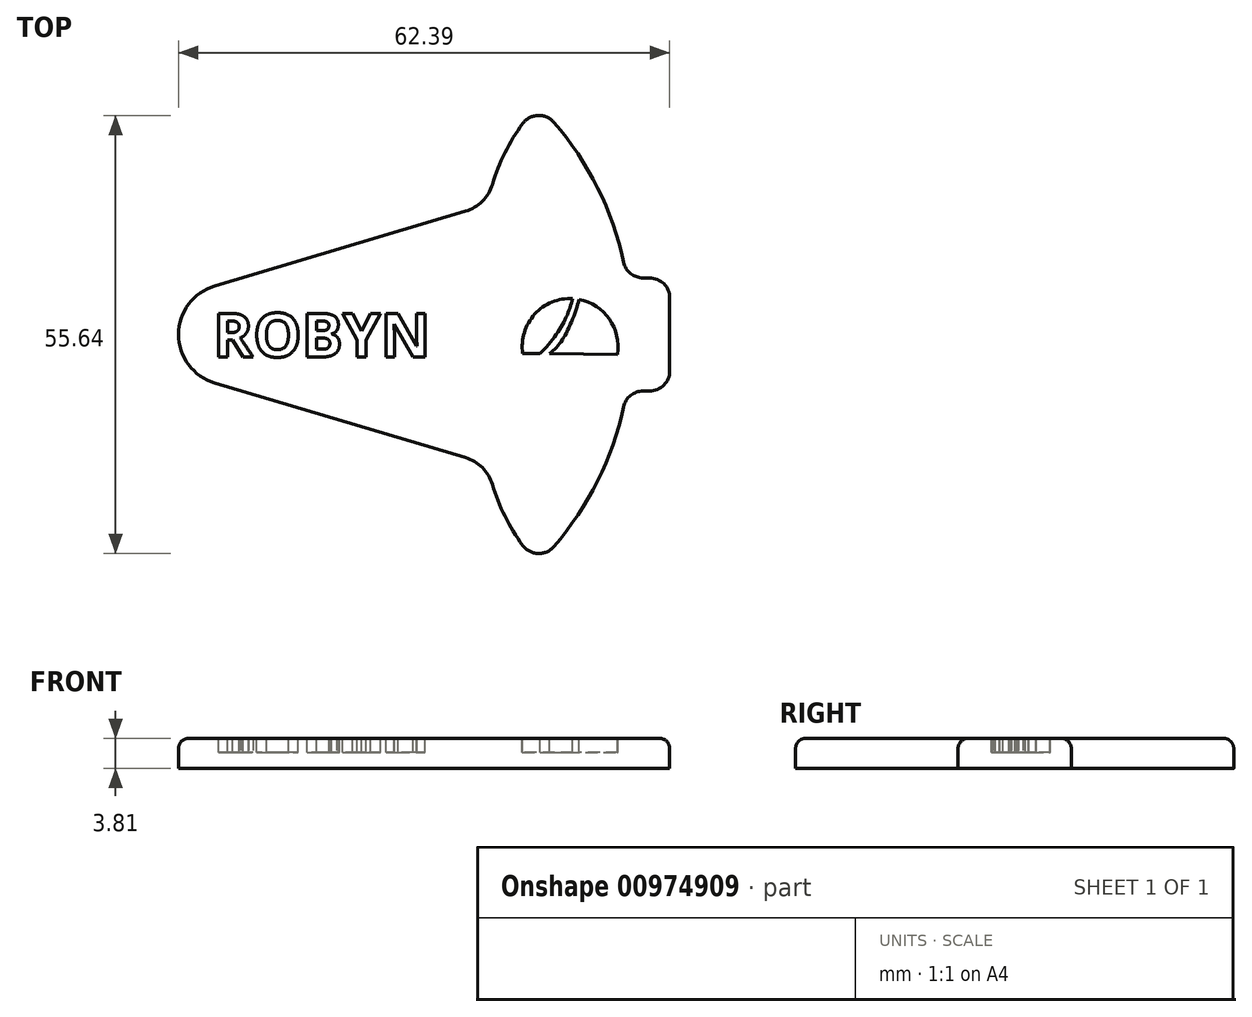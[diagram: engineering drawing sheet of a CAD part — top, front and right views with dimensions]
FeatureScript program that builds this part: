
annotation { "Feature Type Name" : "Feature", "Feature Type Description" : "" }
export const myFeature = defineFeature(function(context is Context, id is Id, definition is map)
    precondition{}
    {
        {
            var Q0;
            Q0=qCreatedBy(makeId("Top.planeOp"),FACE);
            var sketch = newSketch(context, id + "F0", { "sketchPlane" : qUnion([Q0])});
            skLineSegment(sketch, "E0", {"start": v(11.89, 15.65) * mm, "end": v(-19.97, 6.16) * mm});
            skArc(sketch, "E1", {"start": v(19.16, 26.79) * mm, "mid": v(16.9, 23.09) * mm, "end": v(15.3, 19.06) * mm});
            skArc(sketch, "E2", {"start": v(31.97, 9.2) * mm, "mid": v(28.67, 18.62) * mm, "end": v(23.13, 26.94) * mm});
            skArc(sketch, "E3.filletArc", {"start": v(23.13, 26.94) * mm, "mid": v(21.1, 27.82) * mm, "end": v(19.16, 26.79) * mm});
            skPoint(sketch, "E4.visualSharp", {"position": v(14.67, 16.48) * mm});
            skArc(sketch, "E4.filletArc", {"start": v(11.89, 15.65) * mm, "mid": v(14.03, 16.92) * mm, "end": v(15.3, 19.06) * mm});
            skLineSegment(sketch, "E5", {"start": v(0, 0) * mm, "end": v(38.6, 0) * mm, "construction": true});
            skLineSegment(sketch, "E6.bottom", {"start": v(35.29, 7.18) * mm, "end": v(34.45, 7.18) * mm});
            skLineSegment(sketch, "E6.left", {"start": v(37.83, 4.64) * mm, "end": v(37.83, 0) * mm});
            skPoint(sketch, "E6.middle", {"position": v(32.86, 0) * mm});
            skPoint(sketch, "E7.newPointB", {"position": v(27.89, 7.18) * mm});
            skArc(sketch, "E7.filletArc", {"start": v(31.97, 9.2) * mm, "mid": v(32.86, 7.75) * mm, "end": v(34.45, 7.18) * mm});
            skPoint(sketch, "E8.visualSharp", {"position": v(37.83, 7.18) * mm});
            skArc(sketch, "E8.filletArc", {"start": v(37.83, 4.64) * mm, "mid": v(37.09, 6.44) * mm, "end": v(35.29, 7.18) * mm});
            skPoint(sketch, "E9.orphan", {"position": v(37.83, -7.18) * mm});
            skLineSegment(sketch, "E10.MirrorCS", {"start": v(11.89, -15.65) * mm, "end": v(-19.97, -6.16) * mm});
            skArc(sketch, "E11.MirrorCS", {"start": v(11.89, -15.65) * mm, "mid": v(14.03, -16.92) * mm, "end": v(15.3, -19.06) * mm});
            skArc(sketch, "E12.MirrorCS", {"start": v(19.16, -26.79) * mm, "mid": v(16.9, -23.09) * mm, "end": v(15.3, -19.06) * mm});
            skArc(sketch, "E13.MirrorCS", {"start": v(23.13, -26.94) * mm, "mid": v(21.1, -27.82) * mm, "end": v(19.16, -26.79) * mm});
            skArc(sketch, "E14.MirrorCS", {"start": v(31.97, -9.2) * mm, "mid": v(28.67, -18.62) * mm, "end": v(23.13, -26.94) * mm});
            skArc(sketch, "E15.MirrorCS", {"start": v(31.97, -9.2) * mm, "mid": v(32.86, -7.75) * mm, "end": v(34.45, -7.18) * mm});
            skLineSegment(sketch, "E16.MirrorCS", {"start": v(35.29, -7.18) * mm, "end": v(34.45, -7.18) * mm});
            skArc(sketch, "E17.MirrorCS", {"start": v(37.83, -4.64) * mm, "mid": v(37.09, -6.44) * mm, "end": v(35.29, -7.18) * mm});
            skLineSegment(sketch, "E18.MirrorCS", {"start": v(37.83, -4.64) * mm, "end": v(37.83, 0) * mm});
            skPoint(sketch, "E19.newPointA", {"position": v(-20.8, 5.9) * mm});
            skPoint(sketch, "E19.newPointB", {"position": v(-20.8, -5.9) * mm});
            skArc(sketch, "E19.filletArc", {"start": v(-19.97, 6.16) * mm, "mid": v(-24.56, 0) * mm, "end": v(-19.97, -6.16) * mm});
            skSolve(sketch);
        }
        {
            var Q0;
            Q0=qSketchRegion(id+"F0",true);
            extrude(context, id + "F1", {"entities" : qUnion([Q0]), "depth" : 3.8 * mm, "offsetDistance" : 25.4 * mm});
        }
        {
            var Q0;
            Q0=makeQuery(id+"F1.opExtrude","CAP_FACE",FACE,{"disambiguationData":[OSD([sQuery(id+"F0.wireOp",EDGE,"E0"),sQuery(id+"F0.wireOp",EDGE,"E1"),sQuery(id+"F0.wireOp",EDGE,"E2"),sQuery(id+"F0.wireOp",EDGE,"E3.filletArc"),sQuery(id+"F0.wireOp",EDGE,"E4.filletArc"),sQuery(id+"F0.wireOp",EDGE,"E6.bottom"),sQuery(id+"F0.wireOp",EDGE,"E6.left"),sQuery(id+"F0.wireOp",EDGE,"E7.filletArc"),sQuery(id+"F0.wireOp",EDGE,"E8.filletArc"),sQuery(id+"F0.wireOp",EDGE,"E10.MirrorCS"),sQuery(id+"F0.wireOp",EDGE,"E11.MirrorCS"),sQuery(id+"F0.wireOp",EDGE,"E12.MirrorCS"),sQuery(id+"F0.wireOp",EDGE,"E13.MirrorCS"),sQuery(id+"F0.wireOp",EDGE,"E14.MirrorCS"),sQuery(id+"F0.wireOp",EDGE,"E15.MirrorCS"),sQuery(id+"F0.wireOp",EDGE,"E16.MirrorCS"),sQuery(id+"F0.wireOp",EDGE,"E17.MirrorCS"),sQuery(id+"F0.wireOp",EDGE,"E18.MirrorCS"),sQuery(id+"F0.wireOp",EDGE,"E19.filletArc")])],"isStart":false});
            var sketch = newSketch(context, id + "F2", { "sketchPlane" : qUnion([Q0])});
            skText(sketch, "E20", { "text": "ROBYN", "fontName": "OpenSans-Bold.ttf"});
            skArc(sketch, "E21", {"start": v(31.17, -2.53) * mm, "mid": v(30.17, 1.95) * mm, "end": v(26.32, 4.45) * mm});
            skLineSegment(sketch, "E22", {"start": v(19.16, -2.42) * mm, "end": v(21.34, -2.44) * mm});
            skFitSpline(sketch, "E23", {"points": [v(21.34, -2.44) * mm, v(24.33, 1.49) * mm, v(25.51, 4.55) * mm], "startDerivative": vector(6.62, 6.16) * mm, "endDerivative": vector(1.74, 6.77) * mm});
            skFitSpline(sketch, "E24", {"points": [v(22.55, -2.45) * mm, v(24.6, 0) * mm, v(26.32, 4.45) * mm], "startDerivative": vector(5.89, 4.59) * mm, "endDerivative": vector(1.7, 6.96) * mm});
            skLineSegment(sketch, "E25.trimOffspring", {"start": v(22.55, -2.45) * mm, "end": v(31.17, -2.53) * mm});
            skArc(sketch, "E26.trimOffspring", {"start": v(25.51, 4.55) * mm, "mid": v(20.68, 2.57) * mm, "end": v(19.16, -2.42) * mm});
            const initialGuessF2  = {"E20": [-0.0202, -0.00285, 1, 0, 0.00558]};
            skSetInitialGuess(sketch, initialGuessF2);
            skSolve(sketch);
        }
        {
            var Q0;
            Q0=qSketchRegion(id+"F2",true);
            extrude(context, id + "F3", {"entities" : qUnion([Q0]), "operationType" : NewBodyOperationType.REMOVE, "oppositeDirection" : true, "depth" : 1.78 * mm, "offsetDistance" : 25.4 * mm});
        }
        {
            var Q0;
            Q0=makeQuery(id+"F1.opExtrude","CAP_EDGE",EDGE,{"disambiguationData":[OSD([sQuery(id+"F0.wireOp",EDGE,"E0")])],"isStart":false});
            fillet(context, id + "F4", {"entities" : qUnion([Q0]), "radius" : 1.27 * mm, "tangentPropagation" : true, "allowEdgeOverflow" : false});
        }
    });
